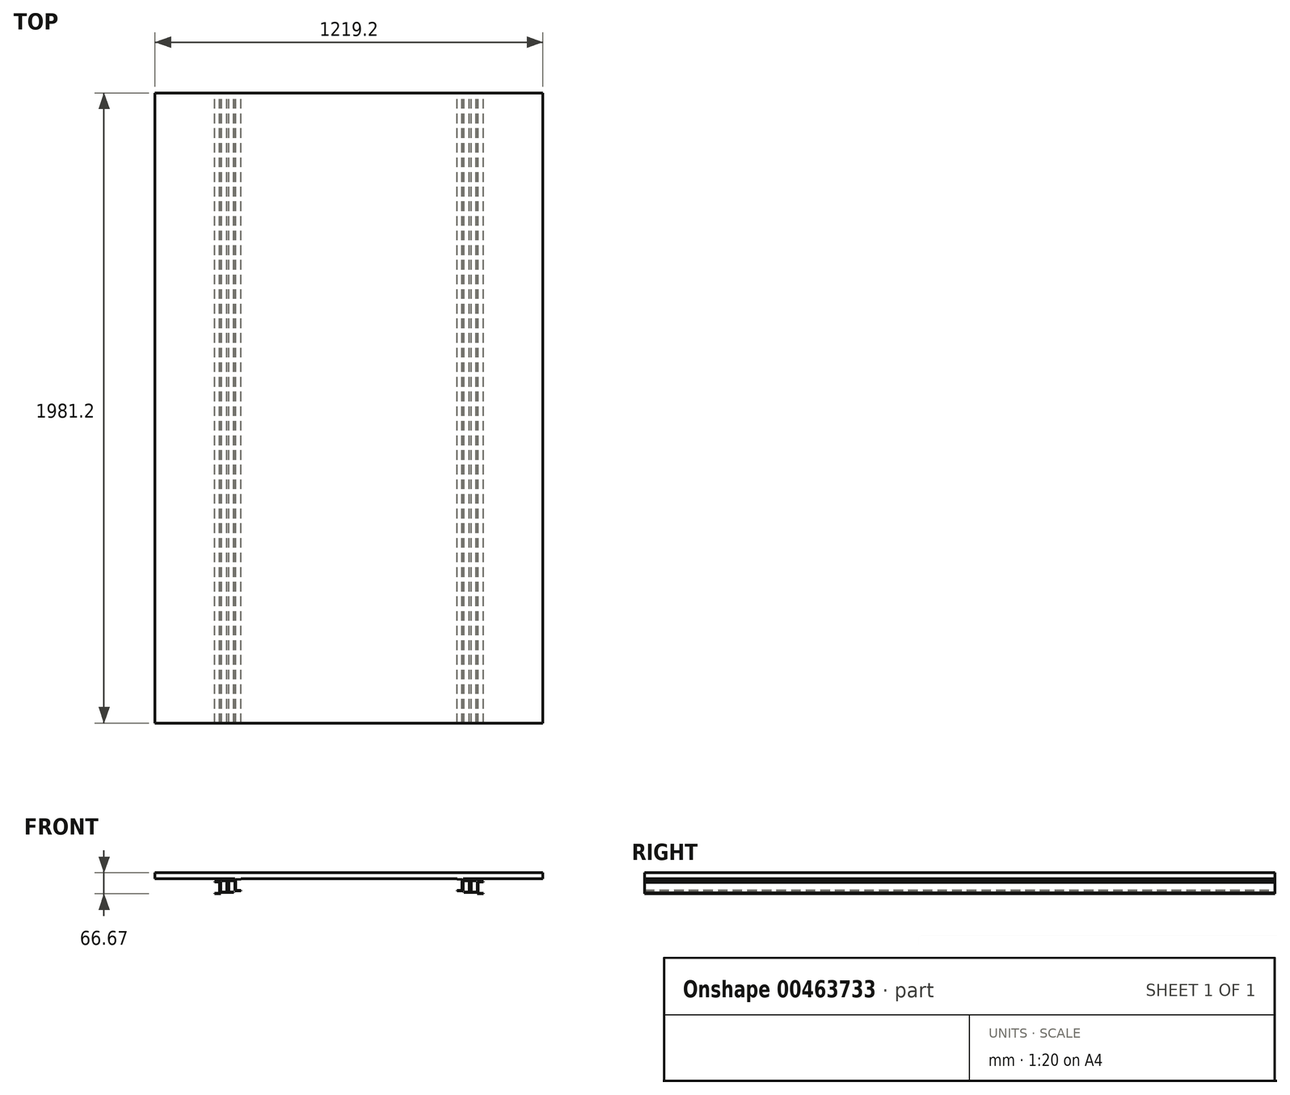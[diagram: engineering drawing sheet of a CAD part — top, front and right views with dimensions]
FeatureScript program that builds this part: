
annotation { "Feature Type Name" : "Feature", "Feature Type Description" : "" }
export const myFeature = defineFeature(function(context is Context, id is Id, definition is map)
    precondition{}
    {
        {
            var Q0;
            Q0=qCreatedBy(makeId("Front.planeOp"),FACE);
            var sketch = newSketch(context, id + "F0", { "sketchPlane" : qUnion([Q0])});
            skLineSegment(sketch, "E0", {"start": v(-27.6, 36.73) * mm, "end": v(-8.56, 36.73) * mm});
            skLineSegment(sketch, "E1", {"start": v(-8.56, 36.73) * mm, "end": v(-8.56, 35.46) * mm});
            skLineSegment(sketch, "E2", {"start": v(-8.56, 35.46) * mm, "end": v(-24.43, 34.07) * mm});
            skLineSegment(sketch, "E3", {"start": v(-24.43, 1.29) * mm, "end": v(-8.56, -0.1) * mm});
            skLineSegment(sketch, "E4", {"start": v(-8.56, -0.1) * mm, "end": v(-8.56, -1.37) * mm});
            skLineSegment(sketch, "E5", {"start": v(-8.56, -1.37) * mm, "end": v(-27.6, -1.37) * mm});
            skLineSegment(sketch, "E6", {"start": v(-27.6, -1.37) * mm, "end": v(-27.6, 36.73) * mm});
            skLineSegment(sketch, "E7", {"start": v(-24.43, 34.07) * mm, "end": v(-24.43, 1.29) * mm});
            skLineSegment(sketch, "E8.MirrorCS", {"start": v(-46.66, 36.73) * mm, "end": v(-46.66, 35.46) * mm});
            skLineSegment(sketch, "E9.MirrorCS", {"start": v(-46.66, -0.1) * mm, "end": v(-46.66, -1.37) * mm});
            skLineSegment(sketch, "E10.MirrorCS", {"start": v(-27.6, 36.73) * mm, "end": v(-46.66, 36.73) * mm});
            skLineSegment(sketch, "E11.MirrorCS", {"start": v(-46.66, -1.37) * mm, "end": v(-27.6, -1.37) * mm});
            skLineSegment(sketch, "E12.MirrorCS", {"start": v(-30.78, 1.29) * mm, "end": v(-46.66, -0.1) * mm});
            skLineSegment(sketch, "E13.MirrorCS", {"start": v(-46.66, 35.46) * mm, "end": v(-30.78, 34.07) * mm});
            skLineSegment(sketch, "E14.MirrorCS", {"start": v(-30.78, 34.07) * mm, "end": v(-30.78, 1.29) * mm});
            skLineSegment(sketch, "E15", {"start": v(353.4, 281.38) * mm, "end": v(353.4, -203.42) * mm, "construction": true});
            skLineSegment(sketch, "E16.bottom", {"start": v(-256.2, 41.5) * mm, "end": v(963, 41.5) * mm});
            skLineSegment(sketch, "E16.top", {"start": v(-256.2, 60.54) * mm, "end": v(963, 60.54) * mm});
            skLineSegment(sketch, "E16.left", {"start": v(-256.2, 41.5) * mm, "end": v(-256.2, 60.54) * mm});
            skLineSegment(sketch, "E16.right", {"start": v(963, 41.5) * mm, "end": v(963, 60.54) * mm});
            skLineSegment(sketch, "E17", {"start": v(-5.38, 41.5) * mm, "end": v(13.67, 41.5) * mm});
            skLineSegment(sketch, "E18", {"start": v(13.67, 41.5) * mm, "end": v(13.67, 40.22) * mm});
            skLineSegment(sketch, "E19", {"start": v(13.67, 40.22) * mm, "end": v(-2.2, 38.83) * mm});
            skLineSegment(sketch, "E20", {"start": v(-2.2, 6.05) * mm, "end": v(13.67, 4.66) * mm});
            skLineSegment(sketch, "E21", {"start": v(13.67, 4.66) * mm, "end": v(13.67, 3.4) * mm});
            skLineSegment(sketch, "E22", {"start": v(13.67, 3.4) * mm, "end": v(-5.38, 3.4) * mm});
            skLineSegment(sketch, "E23", {"start": v(-5.38, 3.4) * mm, "end": v(-5.38, 41.5) * mm});
            skLineSegment(sketch, "E24", {"start": v(-2.2, 38.83) * mm, "end": v(-2.2, 6.05) * mm});
            skLineSegment(sketch, "E25", {"start": v(-561.5, -6.13) * mm, "end": v(1151.53, -6.13) * mm, "construction": true});
            skLineSegment(sketch, "E26", {"start": v(-49.83, -6.13) * mm, "end": v(-49.83, 31.97) * mm});
            skLineSegment(sketch, "E27.MirrorCS", {"start": v(-68.88, 31.97) * mm, "end": v(-68.88, 30.7) * mm});
            skLineSegment(sketch, "E28.MirrorCS", {"start": v(-68.88, -4.86) * mm, "end": v(-68.88, -6.13) * mm});
            skLineSegment(sketch, "E29.MirrorCS", {"start": v(-49.83, 31.97) * mm, "end": v(-68.88, 31.97) * mm});
            skLineSegment(sketch, "E30.MirrorCS", {"start": v(-68.88, -6.13) * mm, "end": v(-49.83, -6.13) * mm});
            skLineSegment(sketch, "E31.MirrorCS", {"start": v(-53, -3.48) * mm, "end": v(-68.88, -4.86) * mm});
            skLineSegment(sketch, "E32.MirrorCS", {"start": v(-68.88, 30.7) * mm, "end": v(-53, 29.3) * mm});
            skLineSegment(sketch, "E33.MirrorCS", {"start": v(-53, 29.3) * mm, "end": v(-53, -3.48) * mm});
            skLineSegment(sketch, "E34.MirrorCS", {"start": v(715.34, -0.1) * mm, "end": v(715.34, -1.37) * mm});
            skLineSegment(sketch, "E35.MirrorCS", {"start": v(693.12, 41.5) * mm, "end": v(693.12, 40.22) * mm});
            skLineSegment(sketch, "E36.MirrorCS", {"start": v(753.44, -0.1) * mm, "end": v(753.44, -1.37) * mm});
            skLineSegment(sketch, "E37.MirrorCS", {"start": v(715.34, 36.73) * mm, "end": v(715.34, 35.46) * mm});
            skLineSegment(sketch, "E38.MirrorCS", {"start": v(693.12, 4.66) * mm, "end": v(693.12, 3.4) * mm});
            skLineSegment(sketch, "E39.MirrorCS", {"start": v(775.67, 31.97) * mm, "end": v(775.67, 30.7) * mm});
            skLineSegment(sketch, "E40.MirrorCS", {"start": v(753.44, 36.73) * mm, "end": v(753.44, 35.46) * mm});
            skLineSegment(sketch, "E41.MirrorCS", {"start": v(775.67, -4.86) * mm, "end": v(775.67, -6.13) * mm});
            skLineSegment(sketch, "E42.MirrorCS", {"start": v(734.4, 36.73) * mm, "end": v(715.34, 36.73) * mm});
            skLineSegment(sketch, "E43.MirrorCS", {"start": v(731.22, 1.29) * mm, "end": v(715.34, -0.1) * mm});
            skLineSegment(sketch, "E44.MirrorCS", {"start": v(715.34, -1.37) * mm, "end": v(734.4, -1.37) * mm});
            skLineSegment(sketch, "E45.MirrorCS", {"start": v(775.67, -6.13) * mm, "end": v(756.62, -6.13) * mm});
            skLineSegment(sketch, "E46.MirrorCS", {"start": v(712.17, 41.5) * mm, "end": v(693.12, 41.5) * mm});
            skLineSegment(sketch, "E47.MirrorCS", {"start": v(734.4, 36.73) * mm, "end": v(753.44, 36.73) * mm});
            skLineSegment(sketch, "E48.MirrorCS", {"start": v(753.44, -1.37) * mm, "end": v(734.4, -1.37) * mm});
            skLineSegment(sketch, "E49.MirrorCS", {"start": v(693.12, 3.4) * mm, "end": v(712.17, 3.4) * mm});
            skLineSegment(sketch, "E50.MirrorCS", {"start": v(759.8, -3.48) * mm, "end": v(775.67, -4.86) * mm});
            skLineSegment(sketch, "E51.MirrorCS", {"start": v(753.44, 35.46) * mm, "end": v(737.57, 34.07) * mm});
            skLineSegment(sketch, "E52.MirrorCS", {"start": v(737.57, 34.07) * mm, "end": v(737.57, 1.29) * mm});
            skLineSegment(sketch, "E53.MirrorCS", {"start": v(709, 38.83) * mm, "end": v(709, 6.05) * mm});
            skLineSegment(sketch, "E54.MirrorCS", {"start": v(709, 6.05) * mm, "end": v(693.12, 4.66) * mm});
            skLineSegment(sketch, "E55.MirrorCS", {"start": v(963, 41.5) * mm, "end": v(-256.2, 41.5) * mm});
            skLineSegment(sketch, "E56.MirrorCS", {"start": v(756.62, 31.97) * mm, "end": v(775.67, 31.97) * mm});
            skLineSegment(sketch, "E57.MirrorCS", {"start": v(715.34, 35.46) * mm, "end": v(731.22, 34.07) * mm});
            skLineSegment(sketch, "E58.MirrorCS", {"start": v(734.4, -1.37) * mm, "end": v(734.4, 36.73) * mm});
            skLineSegment(sketch, "E59.MirrorCS", {"start": v(731.22, 34.07) * mm, "end": v(731.22, 1.29) * mm});
            skLineSegment(sketch, "E60.MirrorCS", {"start": v(737.57, 1.29) * mm, "end": v(753.44, -0.1) * mm});
            skLineSegment(sketch, "E61.MirrorCS", {"start": v(712.17, 3.4) * mm, "end": v(712.17, 41.5) * mm});
            skLineSegment(sketch, "E62.MirrorCS", {"start": v(693.12, 40.22) * mm, "end": v(709, 38.83) * mm});
            skLineSegment(sketch, "E63.MirrorCS", {"start": v(775.67, 30.7) * mm, "end": v(759.8, 29.3) * mm});
            skLineSegment(sketch, "E64.MirrorCS", {"start": v(756.62, -6.13) * mm, "end": v(756.62, 31.97) * mm});
            skLineSegment(sketch, "E65.MirrorCS", {"start": v(759.8, 29.3) * mm, "end": v(759.8, -3.48) * mm});
            skSolve(sketch);
        }
        {
            var Q0;
            Q0 = qSketchRegion(id + "F0", true);
            extrude(context, id + "F1", {"entities" : qUnion([Q0]), "depth" : 1981.2 * mm});
        }
    });
